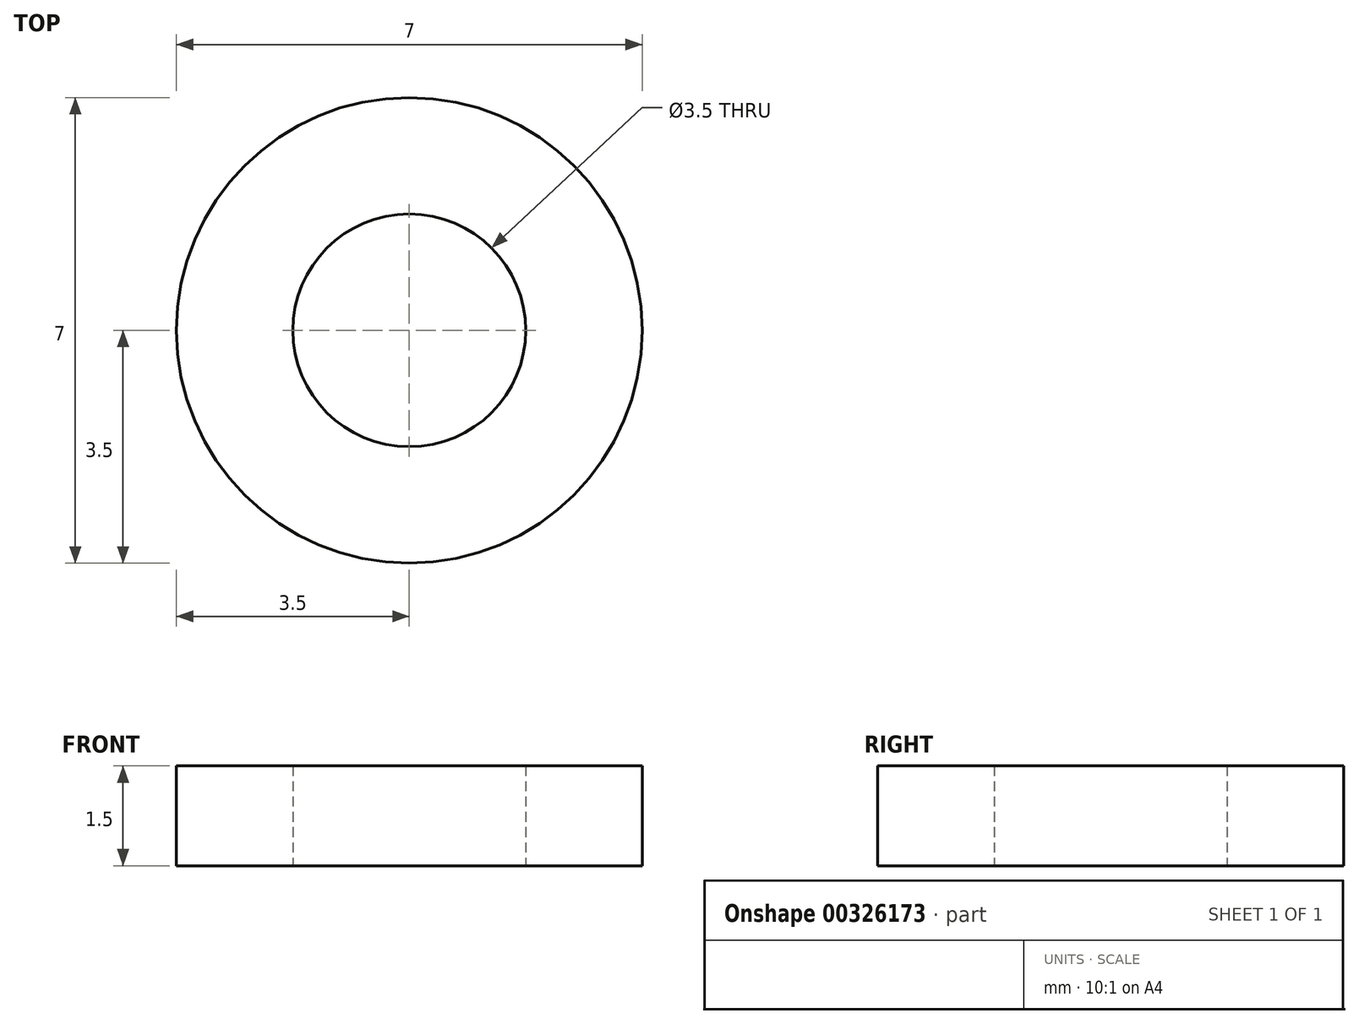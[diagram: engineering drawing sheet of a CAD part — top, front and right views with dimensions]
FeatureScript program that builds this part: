
annotation { "Feature Type Name" : "Feature", "Feature Type Description" : "" }
export const myFeature = defineFeature(function(context is Context, id is Id, definition is map)
    precondition{}
    {
        {
            var Q0;
            Q0=qCreatedBy(makeId("Top.planeOp"),FACE);
            var sketch = newSketch(context, id + "F0", { "sketchPlane" : qUnion([Q0])});
            skCircle(sketch, "E0", {"center": v(0, 0) * mm, "radius": 1.75 * mm});
            skCircle(sketch, "E1", {"center": v(0, 0) * mm, "radius": 3.5 * mm});
            skSolve(sketch);
        }
        {
            var Q0;
            Q0=makeQuery(id+"F0.imprint","IMPRINT",FACE,{"disambiguationData":[TD([[makeQuery(id+"F0.imprint","IMPRINT",EDGE,{"derivedFrom":sQuery(id+"F0.wireOp",EDGE,"E0")}),-1.0]])]});
            extrude(context, id + "F1", {"entities" : qUnion([Q0]), "depth" : 1.5 * mm});
        }
    });
